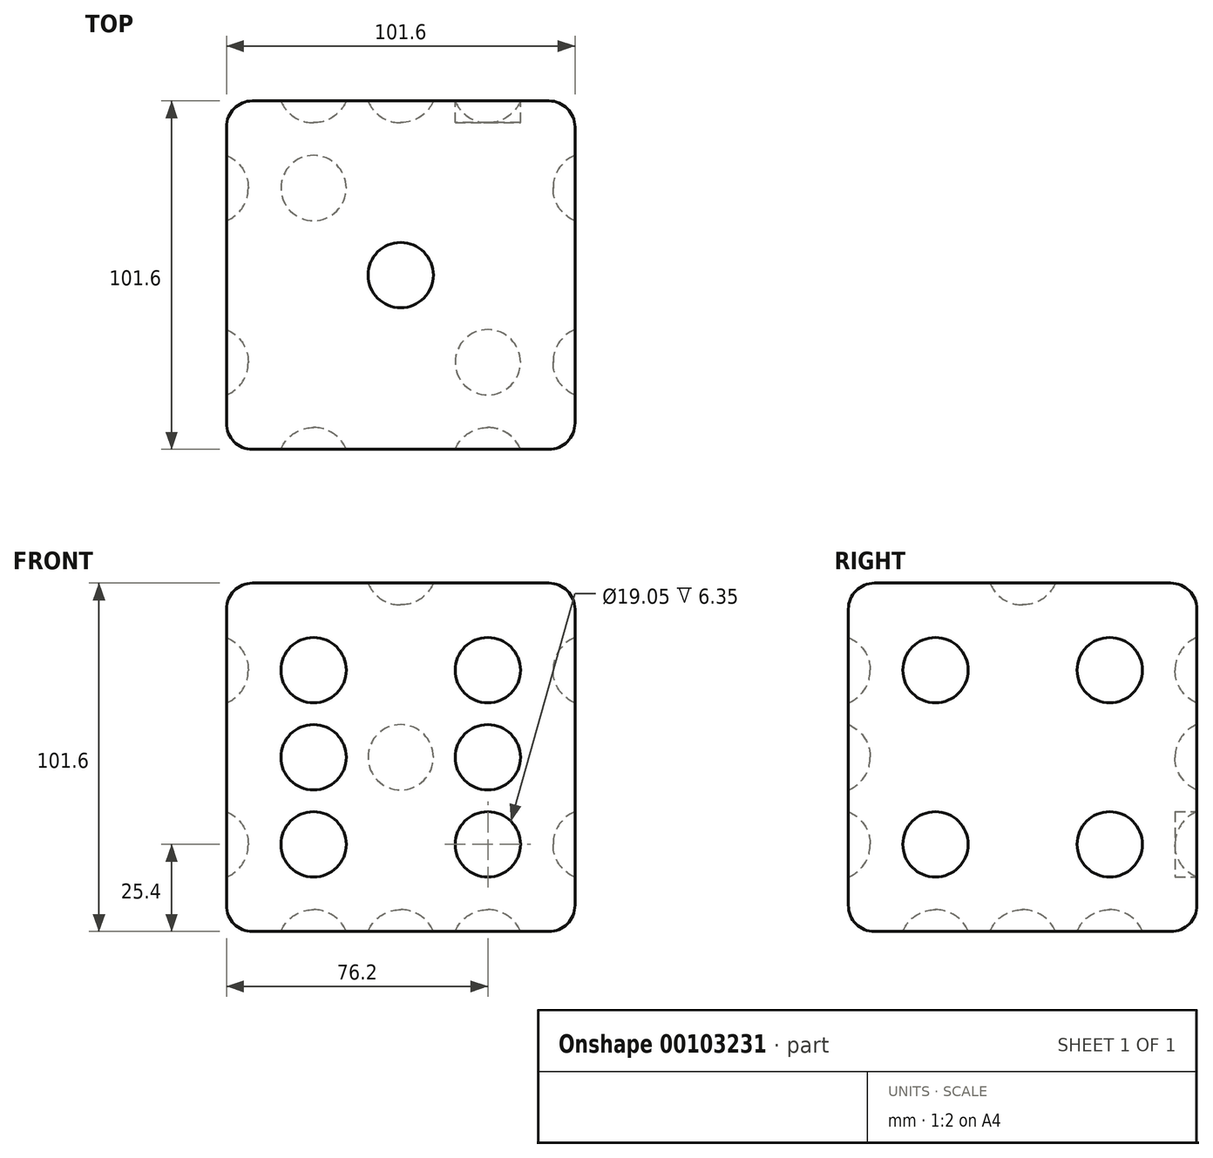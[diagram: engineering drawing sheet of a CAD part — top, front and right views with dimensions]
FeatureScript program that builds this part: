
annotation { "Feature Type Name" : "Feature", "Feature Type Description" : "" }
export const myFeature = defineFeature(function(context is Context, id is Id, definition is map)
    precondition{}
    {
        {
            var Q0;
            Q0=qCreatedBy(makeId("Top.planeOp"),FACE);
            var sketch = newSketch(context, id + "F0", { "sketchPlane" : qUnion([Q0])});
            skLineSegment(sketch, "E0.bottom", {"start": v(-45.9, 54.37) * mm, "end": v(55.7, 54.37) * mm});
            skLineSegment(sketch, "E0.top", {"start": v(-45.9, -47.23) * mm, "end": v(55.7, -47.23) * mm});
            skLineSegment(sketch, "E0.left", {"start": v(-45.9, 54.37) * mm, "end": v(-45.9, -47.23) * mm});
            skLineSegment(sketch, "E0.right", {"start": v(55.7, 54.37) * mm, "end": v(55.7, -47.23) * mm});
            skLineSegment(sketch, "E1", {"start": v(-45.9, 54.37) * mm, "end": v(55.7, -47.23) * mm, "construction": true});
            skLineSegment(sketch, "E2", {"start": v(-45.9, -47.23) * mm, "end": v(55.7, 54.37) * mm, "construction": true});
            skCircle(sketch, "E3", {"center": v(4.9, 3.57) * mm, "radius": 9.53 * mm});
            skSolve(sketch);
        }
        {
            var Q0;
            Q0=makeQuery(id+"F0.imprint","IMPRINT",FACE,{"disambiguationData":[TD([[makeQuery(id+"F0.imprint","IMPRINT",EDGE,{"derivedFrom":sQuery(id+"F0.wireOp",EDGE,"E0.bottom")}),-1.0]])]});
            var Q1;
            Q1=makeQuery(id+"F0.imprint","IMPRINT",FACE,{"disambiguationData":[TD([[makeQuery(id+"F0.imprint","IMPRINT",EDGE,{"derivedFrom":sQuery(id+"F0.wireOp",EDGE,"E3")}),1.0]])]});
            extrude(context, id + "F1", {"entities" : qUnion([Q0, Q1]), "depth" : 101.6 * mm});
        }
        {
            var Q0;
            Q0=makeQuery(id+"F1.opExtrude","CAP_FACE",FACE,{"disambiguationData":[OSD([sQuery(id+"F0.wireOp",EDGE,"E0.bottom"),sQuery(id+"F0.wireOp",EDGE,"E0.top"),sQuery(id+"F0.wireOp",EDGE,"E0.left"),sQuery(id+"F0.wireOp",EDGE,"E0.right")])],"isStart":false});
            var sketch = newSketch(context, id + "F2", { "sketchPlane" : qUnion([Q0])});
            skLineSegment(sketch, "E4", {"start": v(-45.9, 3.57) * mm, "end": v(55.7, 3.57) * mm, "construction": true});
            skCircle(sketch, "E5", {"center": v(4.9, 3.57) * mm, "radius": 9.53 * mm});
            skSolve(sketch);
        }
        {
            var Q0;
            Q0=makeQuery(id+"F2.imprint","IMPRINT",FACE,{"disambiguationData":[TD([[makeQuery(id+"F2.imprint","IMPRINT",EDGE,{"derivedFrom":sQuery(id+"F2.wireOp",EDGE,"E5")}),1.0]])]});
            extrude(context, id + "F3", {"entities" : qUnion([Q0]), "operationType" : NewBodyOperationType.REMOVE, "oppositeDirection" : true, "depth" : 6.35 * mm});
        }
        {
            var Q0;
            Q0=makeQuery(id+"F3.boolean.opBoolean","COPY",EDGE,{"derivedFrom":makeQuery(id+"F3.opExtrude","CAP_EDGE",EDGE,{"disambiguationData":[OSD([sQuery(id+"F2.wireOp",EDGE,"E5")])],"isStart":false})});
            fillet(context, id + "F4", {"entities" : qUnion([Q0]), "radius" : 10.16 * mm, "tangentPropagation" : true, "allowEdgeOverflow" : false});
        }
        {
            var Q0;
            Q0=makeQuery(id+"F1.opExtrude","SWEPT_FACE",FACE,{"disambiguationData":[OSD([sQuery(id+"F0.wireOp",EDGE,"E0.left")])]});
            var sketch = newSketch(context, id + "F5", { "sketchPlane" : qUnion([Q0])});
            skPoint(sketch, "E6.orphan", {"position": v(-3.57, 0) * mm});
            skCircle(sketch, "E7", {"center": v(21.83, 76.2) * mm, "radius": 9.53 * mm});
            skCircle(sketch, "E8", {"center": v(-28.97, 25.4) * mm, "radius": 9.53 * mm});
            skSolve(sketch);
        }
        {
            var Q0;
            Q0=makeQuery(id+"F5.imprint","IMPRINT",FACE,{"disambiguationData":[TD([[makeQuery(id+"F5.imprint","IMPRINT",EDGE,{"derivedFrom":sQuery(id+"F5.wireOp",EDGE,"E8")}),1.0]])]});
            var Q1;
            Q1=makeQuery(id+"F5.imprint","IMPRINT",FACE,{"disambiguationData":[TD([[makeQuery(id+"F5.imprint","IMPRINT",EDGE,{"derivedFrom":sQuery(id+"F5.wireOp",EDGE,"E7")}),1.0]])]});
            extrude(context, id + "F6", {"entities" : qUnion([Q0, Q1]), "operationType" : NewBodyOperationType.REMOVE, "oppositeDirection" : true, "depth" : 6.35 * mm});
        }
        {
            var Q0;
            Q0=makeQuery(id+"F6.boolean.opBoolean","COPY",FACE,{"derivedFrom":makeQuery(id+"F6.opExtrude","CAP_FACE",FACE,{"disambiguationData":[OSD([sQuery(id+"F5.wireOp",EDGE,"E8")])],"isStart":false})});
            var Q1;
            Q1=makeQuery(id+"F6.boolean.opBoolean","COPY",FACE,{"derivedFrom":makeQuery(id+"F6.opExtrude","CAP_FACE",FACE,{"disambiguationData":[OSD([sQuery(id+"F5.wireOp",EDGE,"E7")])],"isStart":false})});
            fillet(context, id + "F7", {"entities" : qUnion([Q0, Q1]), "radius" : 10.16 * mm, "tangentPropagation" : true, "allowEdgeOverflow" : false});
        }
        {
            var Q0;
            Q0=makeQuery(id+"F1.opExtrude","CAP_FACE",FACE,{"disambiguationData":[OSD([sQuery(id+"F0.wireOp",EDGE,"E0.bottom"),sQuery(id+"F0.wireOp",EDGE,"E0.top"),sQuery(id+"F0.wireOp",EDGE,"E0.left"),sQuery(id+"F0.wireOp",EDGE,"E0.right")])],"isStart":true});
            var sketch = newSketch(context, id + "F8", { "sketchPlane" : qUnion([Q0])});
            skCircle(sketch, "E9", {"center": v(4.9, -3.57) * mm, "radius": 9.53 * mm});
            skPoint(sketch, "E10.orphan", {"position": v(-45.9, -54.37) * mm});
            skCircle(sketch, "E11", {"center": v(30.3, 21.83) * mm, "radius": 9.53 * mm});
            skCircle(sketch, "E12", {"center": v(-20.5, -28.97) * mm, "radius": 9.53 * mm});
            skSolve(sketch);
        }
        {
            var Q0;
            Q0 = qSketchRegion(id + "F8", true);
            extrude(context, id + "F9", {"entities" : qUnion([Q0]), "operationType" : NewBodyOperationType.REMOVE, "oppositeDirection" : true, "depth" : 6.35 * mm});
        }
        {
            var Q0;
            Q0=makeQuery(id+"F9.boolean.opBoolean","COPY",FACE,{"derivedFrom":makeQuery(id+"F9.opExtrude","CAP_FACE",FACE,{"disambiguationData":[OSD([sQuery(id+"F8.wireOp",EDGE,"E12")])],"isStart":false})});
            var Q1;
            Q1=makeQuery(id+"F9.boolean.opBoolean","COPY",FACE,{"derivedFrom":makeQuery(id+"F9.opExtrude","CAP_FACE",FACE,{"disambiguationData":[OSD([sQuery(id+"F8.wireOp",EDGE,"E9")])],"isStart":false})});
            var Q2;
            Q2=makeQuery(id+"F9.boolean.opBoolean","COPY",FACE,{"derivedFrom":makeQuery(id+"F9.opExtrude","CAP_FACE",FACE,{"disambiguationData":[OSD([sQuery(id+"F8.wireOp",EDGE,"E11")])],"isStart":false})});
            fillet(context, id + "F10", {"entities" : qUnion([Q0, Q1, Q2]), "radius" : 10.16 * mm, "tangentPropagation" : true, "allowEdgeOverflow" : false});
        }
        {
            var Q0;
            Q0=makeQuery(id+"F1.opExtrude","SWEPT_FACE",FACE,{"disambiguationData":[OSD([sQuery(id+"F0.wireOp",EDGE,"E0.right")])]});
            var sketch = newSketch(context, id + "F11", { "sketchPlane" : qUnion([Q0])});
            skPoint(sketch, "E13.orphan", {"position": v(54.37, 50.8) * mm});
            skCircle(sketch, "E14", {"center": v(-21.83, 25.4) * mm, "radius": 9.53 * mm});
            skCircle(sketch, "E15", {"center": v(-21.83, 76.2) * mm, "radius": 9.53 * mm});
            skCircle(sketch, "E16", {"center": v(28.97, 25.4) * mm, "radius": 9.53 * mm});
            skCircle(sketch, "E17", {"center": v(28.97, 76.2) * mm, "radius": 9.53 * mm});
            skSolve(sketch);
        }
        {
            var Q0;
            Q0 = qSketchRegion(id + "F11", true);
            extrude(context, id + "F12", {"entities" : qUnion([Q0]), "operationType" : NewBodyOperationType.REMOVE, "oppositeDirection" : true, "depth" : 6.35 * mm});
        }
        {
            var Q0;
            Q0=makeQuery(id+"F12.boolean.opBoolean","COPY",FACE,{"derivedFrom":makeQuery(id+"F12.opExtrude","CAP_FACE",FACE,{"disambiguationData":[OSD([sQuery(id+"F11.wireOp",EDGE,"E16")])],"isStart":false})});
            var Q1;
            Q1=makeQuery(id+"F12.boolean.opBoolean","COPY",FACE,{"derivedFrom":makeQuery(id+"F12.opExtrude","CAP_FACE",FACE,{"disambiguationData":[OSD([sQuery(id+"F11.wireOp",EDGE,"E17")])],"isStart":false})});
            var Q2;
            Q2=makeQuery(id+"F12.boolean.opBoolean","COPY",FACE,{"derivedFrom":makeQuery(id+"F12.opExtrude","CAP_FACE",FACE,{"disambiguationData":[OSD([sQuery(id+"F11.wireOp",EDGE,"E15")])],"isStart":false})});
            var Q3;
            Q3=makeQuery(id+"F12.boolean.opBoolean","COPY",FACE,{"derivedFrom":makeQuery(id+"F12.opExtrude","CAP_FACE",FACE,{"disambiguationData":[OSD([sQuery(id+"F11.wireOp",EDGE,"E14")])],"isStart":false})});
            fillet(context, id + "F13", {"entities" : qUnion([Q0, Q1, Q2, Q3]), "radius" : 10.16 * mm, "tangentPropagation" : true, "allowEdgeOverflow" : false});
        }
        {
            var Q0;
            Q0=makeQuery(id+"F1.opExtrude","SWEPT_FACE",FACE,{"disambiguationData":[OSD([sQuery(id+"F0.wireOp",EDGE,"E0.bottom")])]});
            var sketch = newSketch(context, id + "F14", { "sketchPlane" : qUnion([Q0])});
            skCircle(sketch, "E18", {"center": v(-4.9, 50.8) * mm, "radius": 9.53 * mm});
            skCircle(sketch, "E19", {"center": v(-30.3, 25.4) * mm, "radius": 9.53 * mm});
            skCircle(sketch, "E20.MirrorC", {"center": v(20.5, 76.2) * mm, "radius": 9.53 * mm});
            skCircle(sketch, "E21", {"center": v(-30.3, 76.2) * mm, "radius": 9.53 * mm});
            skCircle(sketch, "E22", {"center": v(20.5, 25.4) * mm, "radius": 9.53 * mm});
            skSolve(sketch);
        }
        {
            var Q0;
            Q0 = qSketchRegion(id + "F14", true);
            extrude(context, id + "F15", {"entities" : qUnion([Q0]), "operationType" : NewBodyOperationType.REMOVE, "oppositeDirection" : true, "depth" : 6.35 * mm});
        }
        {
            var Q0;
            Q0=makeQuery(id+"F15.boolean.opBoolean","COPY",FACE,{"derivedFrom":makeQuery(id+"F15.opExtrude","CAP_FACE",FACE,{"disambiguationData":[OSD([sQuery(id+"F14.wireOp",EDGE,"E22")])],"isStart":false})});
            var Q1;
            Q1=makeQuery(id+"F15.boolean.opBoolean","COPY",FACE,{"derivedFrom":makeQuery(id+"F15.opExtrude","CAP_FACE",FACE,{"disambiguationData":[OSD([sQuery(id+"F14.wireOp",EDGE,"E18")])],"isStart":false})});
            var Q2;
            Q2=makeQuery(id+"F15.boolean.opBoolean","COPY",FACE,{"derivedFrom":makeQuery(id+"F15.opExtrude","CAP_FACE",FACE,{"disambiguationData":[OSD([sQuery(id+"F14.wireOp",EDGE,"E20.MirrorC")])],"isStart":false})});
            var Q3;
            Q3=makeQuery(id+"F15.boolean.opBoolean","COPY",FACE,{"derivedFrom":makeQuery(id+"F15.opExtrude","CAP_FACE",FACE,{"disambiguationData":[OSD([sQuery(id+"F14.wireOp",EDGE,"E21")])],"isStart":false})});
            var Q4;
            Q4=makeQuery(id+"F15.boolean.opBoolean","COPY",FACE,{"derivedFrom":makeQuery(id+"F15.opExtrude","CAP_FACE",FACE,{"disambiguationData":[OSD([sQuery(id+"F14.wireOp",EDGE,"E19")])],"isStart":false})});
            fillet(context, id + "F16", {"entities" : qUnion([Q0, Q1, Q2, Q3, Q4]), "radius" : 10.16 * mm, "tangentPropagation" : true, "allowEdgeOverflow" : false});
        }
        {
            var Q0;
            Q0=makeQuery(id+"F1.opExtrude","SWEPT_FACE",FACE,{"disambiguationData":[OSD([sQuery(id+"F0.wireOp",EDGE,"E0.top")])]});
            var sketch = newSketch(context, id + "F17", { "sketchPlane" : qUnion([Q0])});
            skPoint(sketch, "E23.orphan", {"position": v(-45.9, 50.8) * mm});
            skCircle(sketch, "E24", {"center": v(30.3, 25.4) * mm, "radius": 9.53 * mm});
            skCircle(sketch, "E25", {"center": v(30.3, 50.8) * mm, "radius": 9.53 * mm});
            skCircle(sketch, "E26", {"center": v(30.3, 76.2) * mm, "radius": 9.53 * mm});
            skCircle(sketch, "E27.MirrorC", {"center": v(-20.5, 25.4) * mm, "radius": 9.53 * mm});
            skCircle(sketch, "E28.MirrorC", {"center": v(-20.5, 50.8) * mm, "radius": 9.53 * mm});
            skCircle(sketch, "E29.MirrorC", {"center": v(-20.5, 76.2) * mm, "radius": 9.53 * mm});
            skSolve(sketch);
        }
        {
            var Q0;
            Q0 = qSketchRegion(id + "F17", true);
            extrude(context, id + "F18", {"entities" : qUnion([Q0]), "operationType" : NewBodyOperationType.REMOVE, "oppositeDirection" : true, "depth" : 6.35 * mm});
        }
        {
            var Q0;
            Q0=makeQuery(id+"F18.boolean.opBoolean","COPY",FACE,{"derivedFrom":makeQuery(id+"F18.opExtrude","CAP_FACE",FACE,{"disambiguationData":[OSD([sQuery(id+"F17.wireOp",EDGE,"E24")])],"isStart":false})});
            var Q1;
            Q1=makeQuery(id+"F18.boolean.opBoolean","COPY",FACE,{"derivedFrom":makeQuery(id+"F18.opExtrude","CAP_FACE",FACE,{"disambiguationData":[OSD([sQuery(id+"F17.wireOp",EDGE,"E25")])],"isStart":false})});
            var Q2;
            Q2=makeQuery(id+"F18.boolean.opBoolean","COPY",FACE,{"derivedFrom":makeQuery(id+"F18.opExtrude","CAP_FACE",FACE,{"disambiguationData":[OSD([sQuery(id+"F17.wireOp",EDGE,"E26")])],"isStart":false})});
            var Q3;
            Q3=makeQuery(id+"F18.boolean.opBoolean","COPY",FACE,{"derivedFrom":makeQuery(id+"F18.opExtrude","CAP_FACE",FACE,{"disambiguationData":[OSD([sQuery(id+"F17.wireOp",EDGE,"E29.MirrorC")])],"isStart":false})});
            var Q4;
            Q4=makeQuery(id+"F18.boolean.opBoolean","COPY",FACE,{"derivedFrom":makeQuery(id+"F18.opExtrude","CAP_FACE",FACE,{"disambiguationData":[OSD([sQuery(id+"F17.wireOp",EDGE,"E28.MirrorC")])],"isStart":false})});
            var Q5;
            Q5=makeQuery(id+"F18.boolean.opBoolean","COPY",FACE,{"derivedFrom":makeQuery(id+"F18.opExtrude","CAP_FACE",FACE,{"disambiguationData":[OSD([sQuery(id+"F17.wireOp",EDGE,"E27.MirrorC")])],"isStart":false})});
            fillet(context, id + "F19", {"entities" : qUnion([Q0, Q1, Q2, Q3, Q4, Q5]), "radius" : 10.16 * mm, "tangentPropagation" : true, "allowEdgeOverflow" : false});
        }
        {
            var Q0;
            Q0=makeQuery(id+"F1.opExtrude","CAP_EDGE",EDGE,{"disambiguationData":[OSD([sQuery(id+"F0.wireOp",EDGE,"E0.right")])],"isStart":false});
            var Q1;
            Q1=makeQuery(id+"F1.opExtrude","CAP_EDGE",EDGE,{"disambiguationData":[OSD([sQuery(id+"F0.wireOp",EDGE,"E0.bottom")])],"isStart":false});
            var Q2;
            Q2=makeQuery(id+"F1.opExtrude","SWEPT_EDGE",EDGE,{"disambiguationData":[OSD([sQuery(id+"F0.wireOp",EDGE,"E0.bottom"),sQuery(id+"F0.wireOp",EDGE,"E0.right")])]});
            var Q3;
            Q3=makeQuery(id+"F1.opExtrude","CAP_EDGE",EDGE,{"disambiguationData":[OSD([sQuery(id+"F0.wireOp",EDGE,"E0.top")])],"isStart":false});
            var Q4;
            Q4=makeQuery(id+"F1.opExtrude","CAP_EDGE",EDGE,{"disambiguationData":[OSD([sQuery(id+"F0.wireOp",EDGE,"E0.left")])],"isStart":false});
            var Q5;
            Q5=makeQuery(id+"F1.opExtrude","CAP_EDGE",EDGE,{"disambiguationData":[OSD([sQuery(id+"F0.wireOp",EDGE,"E0.right")])],"isStart":true});
            var Q6;
            Q6=makeQuery(id+"F1.opExtrude","CAP_EDGE",EDGE,{"disambiguationData":[OSD([sQuery(id+"F0.wireOp",EDGE,"E0.bottom")])],"isStart":true});
            var Q7;
            Q7=makeQuery(id+"F1.opExtrude","CAP_EDGE",EDGE,{"disambiguationData":[OSD([sQuery(id+"F0.wireOp",EDGE,"E0.top")])],"isStart":true});
            var Q8;
            Q8=makeQuery(id+"F1.opExtrude","CAP_EDGE",EDGE,{"disambiguationData":[OSD([sQuery(id+"F0.wireOp",EDGE,"E0.left")])],"isStart":true});
            var Q9;
            Q9=makeQuery(id+"F1.opExtrude","SWEPT_EDGE",EDGE,{"disambiguationData":[OSD([sQuery(id+"F0.wireOp",EDGE,"E0.top"),sQuery(id+"F0.wireOp",EDGE,"E0.right")])]});
            var Q10;
            Q10=makeQuery(id+"F1.opExtrude","SWEPT_EDGE",EDGE,{"disambiguationData":[OSD([sQuery(id+"F0.wireOp",EDGE,"E0.top"),sQuery(id+"F0.wireOp",EDGE,"E0.left")])]});
            var Q11;
            Q11=makeQuery(id+"F1.opExtrude","SWEPT_EDGE",EDGE,{"disambiguationData":[OSD([sQuery(id+"F0.wireOp",EDGE,"E0.bottom"),sQuery(id+"F0.wireOp",EDGE,"E0.left")])]});
            fillet(context, id + "F20", {"entities" : qUnion([Q0, Q1, Q2, Q3, Q4, Q5, Q6, Q7, Q8, Q9, Q10, Q11]), "radius" : 7.62 * mm, "tangentPropagation" : true, "allowEdgeOverflow" : false});
        }
    });
